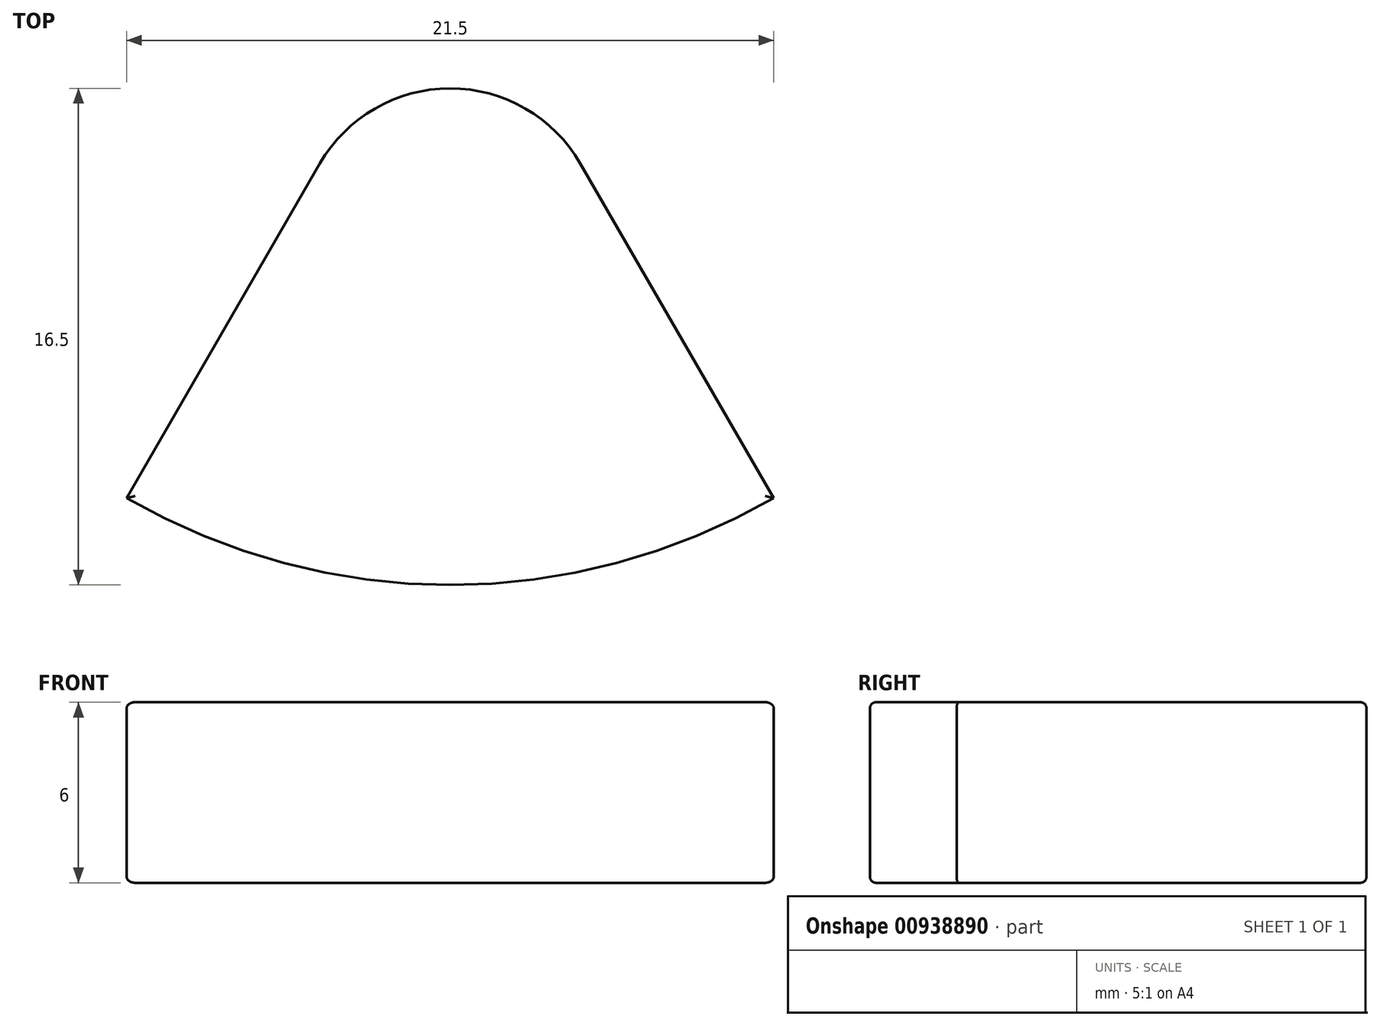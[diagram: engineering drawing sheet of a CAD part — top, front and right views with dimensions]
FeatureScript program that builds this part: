
annotation { "Feature Type Name" : "Feature", "Feature Type Description" : "" }
export const myFeature = defineFeature(function(context is Context, id is Id, definition is map)
    precondition{}
    {
        {
            var Q0;
            Q0=qCreatedBy(makeId("Top.planeOp"),FACE);
            var sketch = newSketch(context, id + "F0", { "sketchPlane" : qUnion([Q0])});
            skLineSegment(sketch, "E0.0", {"start": v(0, 0) * mm, "end": v(10.75, -18.62) * mm});
            skLineSegment(sketch, "E0.2", {"start": v(-10.75, -18.62) * mm, "end": v(0, 0) * mm});
            skArc(sketch, "E1", {"start": v(-10.75, -18.62) * mm, "mid": v(0, -21.5) * mm, "end": v(10.75, -18.62) * mm});
            skPoint(sketch, "E0.cCircle.center.orphan", {"position": v(0, -35) * mm});
            skSolve(sketch);
        }
        {
            var Q0;
            Q0=makeQuery(id+"F0.imprint","IMPRINT",FACE,{"disambiguationData":[TD([[makeQuery(id+"F0.imprint","IMPRINT",EDGE,{"derivedFrom":sQuery(id+"F0.wireOp",EDGE,"E0.0")}),-1.0]])]});
            extrude(context, id + "F1", {"entities" : qUnion([Q0]), "depth" : 6 * mm, "offsetDistance" : 25 * mm});
        }
        {
            var Q0;
            Q0=makeQuery(id+"F1.opExtrude","SWEPT_EDGE",EDGE,{"disambiguationData":[OSD([sQuery(id+"F0.wireOp",EDGE,"E0.0"),sQuery(id+"F0.wireOp",EDGE,"E0.2")])]});
            fillet(context, id + "F2", {"entities" : qUnion([Q0]), "radius" : 5 * mm, "tangentPropagation" : true, "allowEdgeOverflow" : false});
        }
        {
            var Q0;
            Q0=makeQuery(id+"F1.opExtrude","CAP_FACE",FACE,{"disambiguationData":[OSD([sQuery(id+"F0.wireOp",EDGE,"E0.0"),sQuery(id+"F0.wireOp",EDGE,"E0.2"),sQuery(id+"F0.wireOp",EDGE,"E1")])],"isStart":false});
            fillet(context, id + "F3", {"entities" : qUnion([Q0]), "radius" : 0.2 * mm, "tangentPropagation" : true, "allowEdgeOverflow" : false});
        }
        {
            var Q0;
            Q0=makeQuery(id+"F1.opExtrude","CAP_FACE",FACE,{"disambiguationData":[OSD([sQuery(id+"F0.wireOp",EDGE,"E0.0"),sQuery(id+"F0.wireOp",EDGE,"E0.2"),sQuery(id+"F0.wireOp",EDGE,"E1")])],"isStart":true});
            fillet(context, id + "F4", {"entities" : qUnion([Q0]), "radius" : 0.2 * mm, "tangentPropagation" : true, "allowEdgeOverflow" : false});
        }
    });
